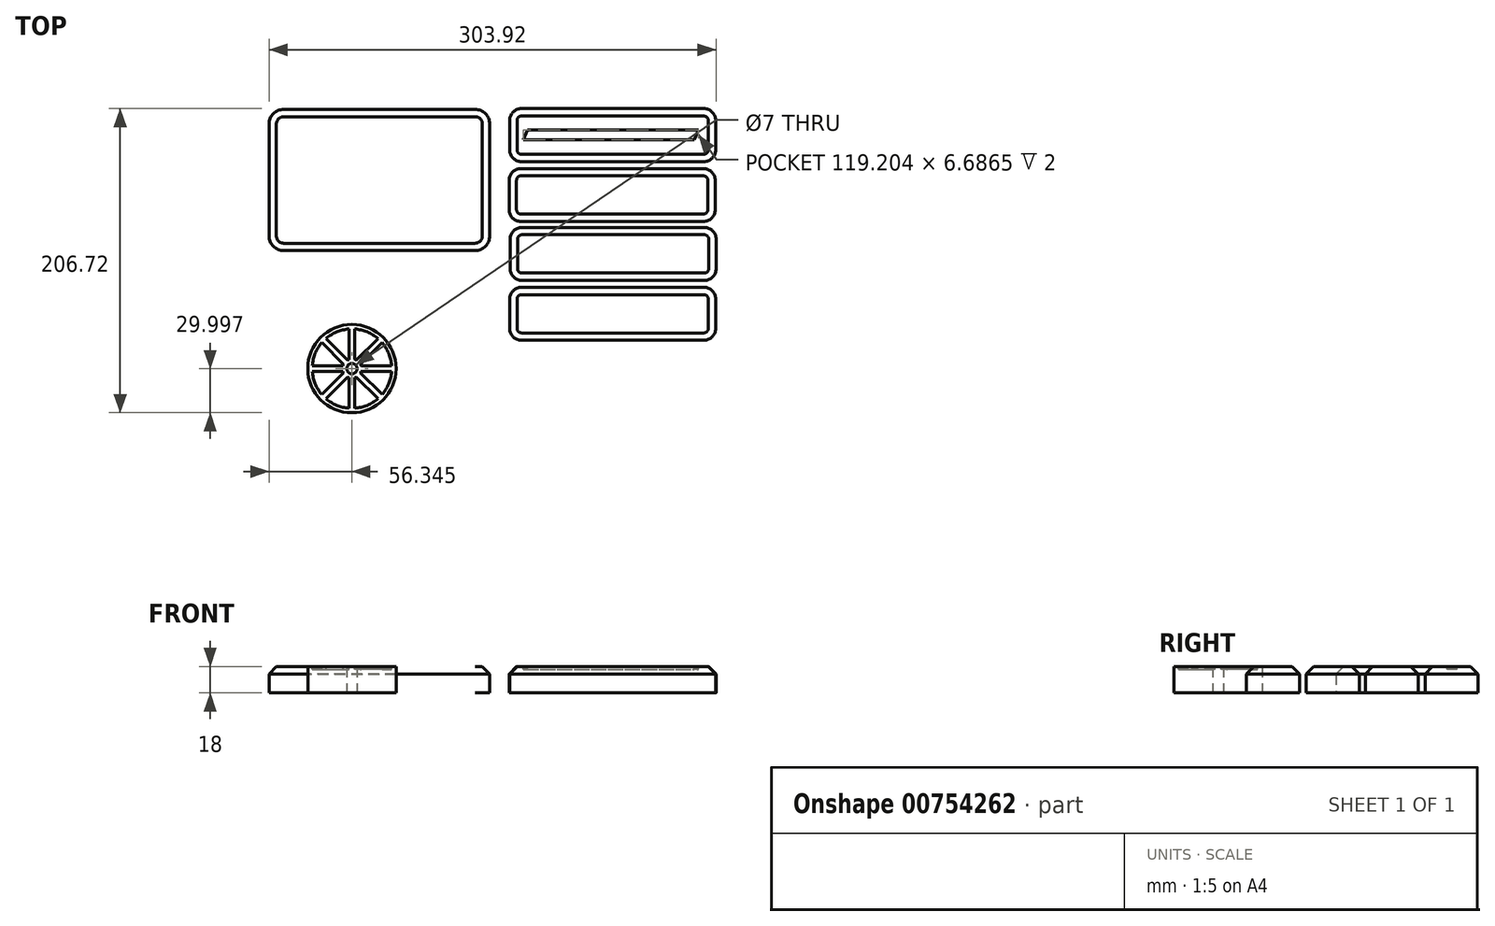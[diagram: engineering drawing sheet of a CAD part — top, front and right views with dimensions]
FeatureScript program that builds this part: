
annotation { "Feature Type Name" : "Feature", "Feature Type Description" : "" }
export const myFeature = defineFeature(function(context is Context, id is Id, definition is map)
    precondition{}
    {
        {
            var Q0;
            Q0=qCreatedBy(makeId("Top.planeOp"),FACE);
            var sketch = newSketch(context, id + "F0", { "sketchPlane" : qUnion([Q0])});
            skLineSegment(sketch, "E0.bottom", {"start": v(-76.14, 52.3) * mm, "end": v(53.86, 52.3) * mm});
            skLineSegment(sketch, "E0.top", {"start": v(-76.14, -43.7) * mm, "end": v(53.86, -43.7) * mm});
            skLineSegment(sketch, "E0.left", {"start": v(-86.14, 42.3) * mm, "end": v(-86.14, -33.7) * mm});
            skLineSegment(sketch, "E0.right", {"start": v(63.86, 42.3) * mm, "end": v(63.86, -33.7) * mm});
            skPoint(sketch, "E1.visualSharp", {"position": v(-86.14, 52.3) * mm});
            skArc(sketch, "E1.filletArc", {"start": v(-76.14, 52.3) * mm, "mid": v(-83.2, 49.38) * mm, "end": v(-86.14, 42.3) * mm});
            skPoint(sketch, "E2.visualSharp", {"position": v(-86.14, -43.7) * mm});
            skArc(sketch, "E2.filletArc", {"start": v(-86.14, -33.7) * mm, "mid": v(-83.2, -40.77) * mm, "end": v(-76.14, -43.7) * mm});
            skPoint(sketch, "E3.visualSharp", {"position": v(63.86, -43.7) * mm});
            skArc(sketch, "E3.filletArc", {"start": v(53.86, -43.7) * mm, "mid": v(60.93, -40.77) * mm, "end": v(63.86, -33.7) * mm});
            skPoint(sketch, "E4.visualSharp", {"position": v(63.86, 52.3) * mm});
            skArc(sketch, "E4.filletArc", {"start": v(63.86, 42.3) * mm, "mid": v(60.93, 49.38) * mm, "end": v(53.86, 52.3) * mm});
            skLineSegment(sketch, "E5.bottom", {"start": v(85.44, 52.8) * mm, "end": v(209.44, 52.8) * mm});
            skLineSegment(sketch, "E5.top", {"start": v(85.44, 16.8) * mm, "end": v(209.44, 16.8) * mm});
            skLineSegment(sketch, "E5.left", {"start": v(77.44, 44.8) * mm, "end": v(77.44, 24.8) * mm});
            skLineSegment(sketch, "E5.right", {"start": v(217.44, 44.8) * mm, "end": v(217.44, 24.8) * mm});
            skPoint(sketch, "E6.visualSharp", {"position": v(77.44, 52.8) * mm});
            skArc(sketch, "E6.filletArc", {"start": v(85.44, 52.8) * mm, "mid": v(79.79, 50.45) * mm, "end": v(77.44, 44.8) * mm});
            skPoint(sketch, "E7.visualSharp", {"position": v(77.44, 16.8) * mm});
            skArc(sketch, "E7.filletArc", {"start": v(77.44, 24.8) * mm, "mid": v(79.79, 19.14) * mm, "end": v(85.44, 16.8) * mm});
            skPoint(sketch, "E8.visualSharp", {"position": v(217.44, 16.8) * mm});
            skArc(sketch, "E8.filletArc", {"start": v(209.44, 16.8) * mm, "mid": v(215.1, 19.14) * mm, "end": v(217.44, 24.8) * mm});
            skPoint(sketch, "E9.visualSharp", {"position": v(217.44, 52.8) * mm});
            skArc(sketch, "E9.filletArc", {"start": v(217.44, 44.8) * mm, "mid": v(215.1, 50.45) * mm, "end": v(209.44, 52.8) * mm});
            skLineSegment(sketch, "E10.bottom", {"start": v(85.1, 12.1) * mm, "end": v(209.1, 12.1) * mm});
            skLineSegment(sketch, "E10.top", {"start": v(85.1, -23.9) * mm, "end": v(209.1, -23.9) * mm});
            skLineSegment(sketch, "E10.left", {"start": v(77.1, 4.1) * mm, "end": v(77.1, -15.9) * mm});
            skLineSegment(sketch, "E10.right", {"start": v(217.1, 4.1) * mm, "end": v(217.1, -15.9) * mm});
            skPoint(sketch, "E11.visualSharp", {"position": v(77.1, 12.1) * mm});
            skArc(sketch, "E11.filletArc", {"start": v(85.1, 12.1) * mm, "mid": v(79.45, 9.76) * mm, "end": v(77.1, 4.1) * mm});
            skPoint(sketch, "E12.visualSharp", {"position": v(77.1, -23.9) * mm});
            skArc(sketch, "E12.filletArc", {"start": v(77.1, -15.9) * mm, "mid": v(79.45, -21.55) * mm, "end": v(85.1, -23.9) * mm});
            skPoint(sketch, "E13.visualSharp", {"position": v(217.1, -23.9) * mm});
            skArc(sketch, "E13.filletArc", {"start": v(209.1, -23.9) * mm, "mid": v(214.76, -21.55) * mm, "end": v(217.1, -15.9) * mm});
            skPoint(sketch, "E14.visualSharp", {"position": v(217.1, 12.1) * mm});
            skArc(sketch, "E14.filletArc", {"start": v(217.1, 4.1) * mm, "mid": v(214.76, 9.76) * mm, "end": v(209.1, 12.1) * mm});
            skLineSegment(sketch, "E15.bottom", {"start": v(85.78, -27.97) * mm, "end": v(209.78, -27.97) * mm});
            skLineSegment(sketch, "E15.top", {"start": v(85.78, -63.97) * mm, "end": v(209.78, -63.97) * mm});
            skLineSegment(sketch, "E15.left", {"start": v(77.78, -35.97) * mm, "end": v(77.78, -55.97) * mm});
            skLineSegment(sketch, "E15.right", {"start": v(217.78, -35.97) * mm, "end": v(217.78, -55.97) * mm});
            skPoint(sketch, "E16.visualSharp", {"position": v(77.78, -27.97) * mm});
            skArc(sketch, "E16.filletArc", {"start": v(85.78, -27.97) * mm, "mid": v(80.13, -30.3) * mm, "end": v(77.78, -35.97) * mm});
            skPoint(sketch, "E17.visualSharp", {"position": v(77.78, -63.97) * mm});
            skArc(sketch, "E17.filletArc", {"start": v(77.78, -55.97) * mm, "mid": v(80.13, -61.62) * mm, "end": v(85.78, -63.97) * mm});
            skPoint(sketch, "E18.visualSharp", {"position": v(217.78, -63.97) * mm});
            skArc(sketch, "E18.filletArc", {"start": v(209.78, -63.97) * mm, "mid": v(215.44, -61.62) * mm, "end": v(217.78, -55.97) * mm});
            skPoint(sketch, "E19.visualSharp", {"position": v(217.78, -27.97) * mm});
            skArc(sketch, "E19.filletArc", {"start": v(217.78, -35.97) * mm, "mid": v(215.44, -30.3) * mm, "end": v(209.78, -27.97) * mm});
            skLineSegment(sketch, "E20.bottom", {"start": v(85.44, -68.65) * mm, "end": v(209.44, -68.65) * mm});
            skLineSegment(sketch, "E20.top", {"start": v(85.44, -104.65) * mm, "end": v(209.44, -104.65) * mm});
            skLineSegment(sketch, "E20.left", {"start": v(77.44, -76.65) * mm, "end": v(77.44, -96.65) * mm});
            skLineSegment(sketch, "E20.right", {"start": v(217.44, -76.65) * mm, "end": v(217.44, -96.65) * mm});
            skPoint(sketch, "E21.visualSharp", {"position": v(77.44, -68.65) * mm});
            skArc(sketch, "E21.filletArc", {"start": v(85.44, -68.65) * mm, "mid": v(79.79, -71) * mm, "end": v(77.44, -76.65) * mm});
            skPoint(sketch, "E22.visualSharp", {"position": v(77.44, -104.65) * mm});
            skArc(sketch, "E22.filletArc", {"start": v(77.44, -96.65) * mm, "mid": v(79.79, -102.31) * mm, "end": v(85.44, -104.65) * mm});
            skPoint(sketch, "E23.visualSharp", {"position": v(217.44, -104.65) * mm});
            skArc(sketch, "E23.filletArc", {"start": v(209.44, -104.65) * mm, "mid": v(215.1, -102.31) * mm, "end": v(217.44, -96.65) * mm});
            skPoint(sketch, "E24.visualSharp", {"position": v(217.44, -68.65) * mm});
            skArc(sketch, "E24.filletArc", {"start": v(217.44, -76.65) * mm, "mid": v(215.1, -71) * mm, "end": v(209.44, -68.65) * mm});
            skSolve(sketch);
        }
        {
            var Q0;
            Q0 = qSketchRegion(id + "F0", true);
            extrude(context, id + "F1", {"entities" : qUnion([Q0]), "depth" : 18 * mm, "offsetDistance" : 25 * mm});
        }
        {
            var Q0;
            Q0=makeQuery(id+"F1.opExtrude","CAP_FACE",FACE,{"disambiguationData":[OSD([sQuery(id+"F0.wireOp",EDGE,"E0.bottom"),sQuery(id+"F0.wireOp",EDGE,"E0.top"),sQuery(id+"F0.wireOp",EDGE,"E0.left"),sQuery(id+"F0.wireOp",EDGE,"E0.right"),sQuery(id+"F0.wireOp",EDGE,"E1.filletArc"),sQuery(id+"F0.wireOp",EDGE,"E2.filletArc"),sQuery(id+"F0.wireOp",EDGE,"E3.filletArc"),sQuery(id+"F0.wireOp",EDGE,"E4.filletArc")])],"isStart":false});
            var Q1;
            Q1=makeQuery(id+"F1.opExtrude","CAP_FACE",FACE,{"disambiguationData":[OSD([sQuery(id+"F0.wireOp",EDGE,"E5.bottom"),sQuery(id+"F0.wireOp",EDGE,"E5.top"),sQuery(id+"F0.wireOp",EDGE,"E5.left"),sQuery(id+"F0.wireOp",EDGE,"E5.right"),sQuery(id+"F0.wireOp",EDGE,"E6.filletArc"),sQuery(id+"F0.wireOp",EDGE,"E7.filletArc"),sQuery(id+"F0.wireOp",EDGE,"E8.filletArc"),sQuery(id+"F0.wireOp",EDGE,"E9.filletArc")])],"isStart":false});
            var Q2;
            Q2=makeQuery(id+"F1.opExtrude","CAP_FACE",FACE,{"disambiguationData":[OSD([sQuery(id+"F0.wireOp",EDGE,"E10.bottom"),sQuery(id+"F0.wireOp",EDGE,"E10.top"),sQuery(id+"F0.wireOp",EDGE,"E10.left"),sQuery(id+"F0.wireOp",EDGE,"E10.right"),sQuery(id+"F0.wireOp",EDGE,"E11.filletArc"),sQuery(id+"F0.wireOp",EDGE,"E12.filletArc"),sQuery(id+"F0.wireOp",EDGE,"E13.filletArc"),sQuery(id+"F0.wireOp",EDGE,"E14.filletArc")])],"isStart":false});
            var Q3;
            Q3=makeQuery(id+"F1.opExtrude","CAP_FACE",FACE,{"disambiguationData":[OSD([sQuery(id+"F0.wireOp",EDGE,"E15.bottom"),sQuery(id+"F0.wireOp",EDGE,"E15.top"),sQuery(id+"F0.wireOp",EDGE,"E15.left"),sQuery(id+"F0.wireOp",EDGE,"E15.right"),sQuery(id+"F0.wireOp",EDGE,"E16.filletArc"),sQuery(id+"F0.wireOp",EDGE,"E17.filletArc"),sQuery(id+"F0.wireOp",EDGE,"E18.filletArc"),sQuery(id+"F0.wireOp",EDGE,"E19.filletArc")])],"isStart":false});
            var Q4;
            Q4=makeQuery(id+"F1.opExtrude","CAP_FACE",FACE,{"disambiguationData":[OSD([sQuery(id+"F0.wireOp",EDGE,"E20.bottom"),sQuery(id+"F0.wireOp",EDGE,"E20.top"),sQuery(id+"F0.wireOp",EDGE,"E20.left"),sQuery(id+"F0.wireOp",EDGE,"E20.right"),sQuery(id+"F0.wireOp",EDGE,"E21.filletArc"),sQuery(id+"F0.wireOp",EDGE,"E22.filletArc"),sQuery(id+"F0.wireOp",EDGE,"E23.filletArc"),sQuery(id+"F0.wireOp",EDGE,"E24.filletArc")])],"isStart":false});
            chamfer(context, id + "F2", {"entities" : qUnion([Q0, Q1, Q2, Q3, Q4]), "width" : 5 * mm, "tangentPropagation" : true});
        }
        {
            var Q0;
            Q0=makeQuery(id+"F1.opExtrude","CAP_FACE",FACE,{"disambiguationData":[OSD([sQuery(id+"F0.wireOp",EDGE,"E5.bottom"),sQuery(id+"F0.wireOp",EDGE,"E5.top"),sQuery(id+"F0.wireOp",EDGE,"E5.left"),sQuery(id+"F0.wireOp",EDGE,"E5.right"),sQuery(id+"F0.wireOp",EDGE,"E6.filletArc"),sQuery(id+"F0.wireOp",EDGE,"E7.filletArc"),sQuery(id+"F0.wireOp",EDGE,"E8.filletArc"),sQuery(id+"F0.wireOp",EDGE,"E9.filletArc")])],"isStart":false});
            var sketch = newSketch(context, id + "F3", { "sketchPlane" : qUnion([Q0])});
            skSolve(sketch);
        }
        {
            var Q0;
            {var subQ0=sQuery(id+"F0.wireOp",EDGE,"E9.filletArc");var subQ1=sQuery(id+"F0.wireOp",EDGE,"E8.filletArc");var subQ2=sQuery(id+"F0.wireOp",EDGE,"E7.filletArc");var subQ3=sQuery(id+"F0.wireOp",EDGE,"E6.filletArc");var subQ4=sQuery(id+"F0.wireOp",EDGE,"E5.right");var subQ5=sQuery(id+"F0.wireOp",EDGE,"E5.left");var subQ6=sQuery(id+"F0.wireOp",EDGE,"E5.top");var subQ7=sQuery(id+"F0.wireOp",EDGE,"E5.bottom");var subQ8=makeQuery(id+"F1.opExtrude","CAP_FACE",FACE,{"disambiguationData":[OSD([subQ7,subQ6,subQ5,subQ4,subQ3,subQ2,subQ1,subQ0])],"isStart":false});Q0=makeQuery(id+"F3.imprint","IMPRINT",FACE,{"disambiguationData":[TD([[makeQuery(id+"F3.imprint","IMPRINT",EDGE,{"derivedFrom":makeQuery(id+"F2.opChamfer","BLEND_EDGE",EDGE,{"blendedFrom":[makeQuery(id+"F1.opExtrude","CAP_EDGE",EDGE,{"disambiguationData":[OSD([subQ7])],"isStart":false}),subQ8],"blendedInto":[subQ8]})}),1.0]])]});}
            var sketch = newSketch(context, id + "F4", { "sketchPlane" : qUnion([Q0])});
            skLineSegment(sketch, "E25", {"start": v(212.5, 34.8) * mm, "end": v(82.44, 34.8) * mm, "construction": true});
            skLineSegment(sketch, "E26", {"start": v(89.67, 38.44) * mm, "end": v(86.67, 31.75) * mm});
            skLineSegment(sketch, "E27", {"start": v(89.67, 38.44) * mm, "end": v(205.88, 38.44) * mm});
            skLineSegment(sketch, "E28", {"start": v(86.67, 31.75) * mm, "end": v(202.87, 31.75) * mm});
            skLineSegment(sketch, "E29", {"start": v(205.88, 38.44) * mm, "end": v(202.87, 31.75) * mm});
            skSolve(sketch);
        }
        {
            var Q0;
            Q0 = qSketchRegion(id + "F4", true);
            extrude(context, id + "F5", {"entities" : qUnion([Q0]), "operationType" : NewBodyOperationType.REMOVE, "oppositeDirection" : true, "depth" : 2 * mm, "offsetDistance" : 25 * mm});
        }
        {
            var Q0;
            Q0=qCreatedBy(makeId("Top.planeOp"),FACE);
            var sketch = newSketch(context, id + "F6", { "sketchPlane" : qUnion([Q0])});
            skCircle(sketch, "E30", {"center": v(-29.8, -123.92) * mm, "radius": 30 * mm});
            skCircle(sketch, "E31", {"center": v(-29.8, -123.92) * mm, "radius": 3.5 * mm});
            skSolve(sketch);
        }
        {
            var Q0;
            Q0 = qSketchRegion(id + "F6", true);
            extrude(context, id + "F7", {"entities" : qUnion([Q0]), "depth" : 18 * mm, "offsetDistance" : 25 * mm});
        }
        {
            var Q0;
            Q0=makeQuery(id+"F7.opExtrude","CAP_FACE",FACE,{"disambiguationData":[OSD([sQuery(id+"F6.wireOp",EDGE,"E30"),sQuery(id+"F6.wireOp",EDGE,"E31")])],"isStart":false});
            var sketch = newSketch(context, id + "F8", { "sketchPlane" : qUnion([Q0])});
            skArc(sketch, "E32", {"start": v(-12.17, -103.47) * mm, "mid": v(-19.46, -98.98) * mm, "end": v(-27.8, -97) * mm});
            skArc(sketch, "E33", {"start": v(-26.84, -118.14) * mm, "mid": v(-27.3, -117.92) * mm, "end": v(-27.8, -117.74) * mm});
            skLineSegment(sketch, "E34", {"start": v(-29.8, -123.92) * mm, "end": v(-29.8, -96.92) * mm, "construction": true});
            skLineSegment(sketch, "E35", {"start": v(-29.8, -123.92) * mm, "end": v(-2.8, -123.92) * mm, "construction": true});
            skLineSegment(sketch, "E36", {"start": v(-29.8, -123.92) * mm, "end": v(-10.7, -104.83) * mm, "construction": true});
            skLineSegment(sketch, "E37", {"start": v(-27.8, -97) * mm, "end": v(-27.8, -117.74) * mm});
            skLineSegment(sketch, "E38", {"start": v(-12.17, -103.47) * mm, "end": v(-26.84, -118.14) * mm});
            skArc(sketch, "E39.trimOffspring", {"start": v(-31.8, -117.74) * mm, "mid": v(-32.28, -117.92) * mm, "end": v(-32.75, -118.14) * mm, "construction": true});
            skArc(sketch, "E40.MirrorCS", {"start": v(-32.75, -118.14) * mm, "mid": v(-32.28, -117.92) * mm, "end": v(-31.8, -117.74) * mm});
            skLineSegment(sketch, "E41.MirrorCS", {"start": v(-31.8, -97) * mm, "end": v(-31.8, -117.74) * mm});
            skLineSegment(sketch, "E42.MirrorCS", {"start": v(-47.42, -103.47) * mm, "end": v(-32.75, -118.14) * mm});
            skArc(sketch, "E43.MirrorCS", {"start": v(-47.42, -103.47) * mm, "mid": v(-40.13, -98.98) * mm, "end": v(-31.8, -97) * mm});
            skArc(sketch, "E44.MirrorCS", {"start": v(-9.34, -106.3) * mm, "mid": v(-4.85, -113.6) * mm, "end": v(-2.87, -121.92) * mm});
            skLineSegment(sketch, "E45.MirrorCS", {"start": v(-9.34, -106.3) * mm, "end": v(-24, -120.96) * mm});
            skArc(sketch, "E46.MirrorCS", {"start": v(-24, -120.96) * mm, "mid": v(-23.79, -121.44) * mm, "end": v(-23.61, -121.92) * mm});
            skLineSegment(sketch, "E47.MirrorCS", {"start": v(-2.87, -121.92) * mm, "end": v(-23.61, -121.92) * mm});
            skLineSegment(sketch, "E48.MirrorCS", {"start": v(-9.34, -141.55) * mm, "end": v(-24, -126.88) * mm});
            skLineSegment(sketch, "E49.MirrorCS", {"start": v(-2.87, -125.92) * mm, "end": v(-23.61, -125.92) * mm});
            skArc(sketch, "E50.MirrorCS", {"start": v(-23.61, -125.92) * mm, "mid": v(-23.79, -126.41) * mm, "end": v(-24, -126.88) * mm});
            skArc(sketch, "E51.MirrorCS", {"start": v(-9.34, -141.55) * mm, "mid": v(-4.85, -134.26) * mm, "end": v(-2.87, -125.92) * mm});
            skArc(sketch, "E52.trimOffspring", {"start": v(-23.61, -121.92) * mm, "mid": v(-23.79, -121.44) * mm, "end": v(-24, -120.96) * mm});
            skPoint(sketch, "E53.orphan", {"position": v(-25.2, -119.33) * mm});
            skPoint(sketch, "E54.orphan", {"position": v(-23.3, -123.92) * mm});
            skArc(sketch, "E55.trimOffspring", {"start": v(-27.8, -117.74) * mm, "mid": v(-27.3, -117.92) * mm, "end": v(-26.84, -118.14) * mm});
            skPoint(sketch, "E56.orphan", {"position": v(-29.8, -117.42) * mm});
            skArc(sketch, "E57.trimOffspring", {"start": v(-24, -126.88) * mm, "mid": v(-23.79, -126.41) * mm, "end": v(-23.61, -125.92) * mm, "construction": true});
            skArc(sketch, "E58.MirrorCS", {"start": v(-12.17, -144.38) * mm, "mid": v(-19.46, -148.87) * mm, "end": v(-27.8, -150.85) * mm});
            skArc(sketch, "E59.MirrorCS", {"start": v(-47.42, -144.38) * mm, "mid": v(-40.13, -148.87) * mm, "end": v(-31.8, -150.85) * mm});
            skLineSegment(sketch, "E60.MirrorCS", {"start": v(-47.42, -144.38) * mm, "end": v(-32.75, -129.71) * mm});
            skLineSegment(sketch, "E61.MirrorCS", {"start": v(-31.8, -150.85) * mm, "end": v(-31.8, -130.1) * mm});
            skLineSegment(sketch, "E62.MirrorCS", {"start": v(-27.8, -150.85) * mm, "end": v(-27.8, -130.1) * mm});
            skLineSegment(sketch, "E63.MirrorCS", {"start": v(-12.17, -144.38) * mm, "end": v(-26.84, -129.71) * mm});
            skArc(sketch, "E64.MirrorCS", {"start": v(-27.8, -130.1) * mm, "mid": v(-27.3, -129.93) * mm, "end": v(-26.84, -129.71) * mm});
            skArc(sketch, "E65.MirrorCS", {"start": v(-32.75, -129.71) * mm, "mid": v(-32.28, -129.93) * mm, "end": v(-31.8, -130.1) * mm});
            skLineSegment(sketch, "E66", {"start": v(-29.8, -123.92) * mm, "end": v(-8.58, -145.14) * mm, "construction": true});
            skArc(sketch, "E67.MirrorCS", {"start": v(-35.98, -125.92) * mm, "mid": v(-35.8, -126.41) * mm, "end": v(-35.58, -126.88) * mm});
            skArc(sketch, "E68.MirrorCS", {"start": v(-35.98, -121.92) * mm, "mid": v(-35.8, -121.44) * mm, "end": v(-35.58, -120.96) * mm});
            skLineSegment(sketch, "E69.MirrorCS", {"start": v(-50.25, -141.55) * mm, "end": v(-35.58, -126.88) * mm});
            skArc(sketch, "E70.MirrorCS", {"start": v(-50.25, -141.55) * mm, "mid": v(-54.74, -134.26) * mm, "end": v(-56.72, -125.92) * mm});
            skLineSegment(sketch, "E71.MirrorCS", {"start": v(-56.72, -125.92) * mm, "end": v(-35.98, -125.92) * mm});
            skLineSegment(sketch, "E72.MirrorCS", {"start": v(-50.25, -106.3) * mm, "end": v(-35.58, -120.96) * mm});
            skLineSegment(sketch, "E73.MirrorCS", {"start": v(-56.72, -121.92) * mm, "end": v(-35.98, -121.92) * mm});
            skArc(sketch, "E74.MirrorCS", {"start": v(-50.25, -106.3) * mm, "mid": v(-54.74, -113.6) * mm, "end": v(-56.72, -121.92) * mm});
            skSolve(sketch);
        }
        {
            var Q0;
            Q0 = qSketchRegion(id + "F8", true);
            extrude(context, id + "F9", {"entities" : qUnion([Q0]), "operationType" : NewBodyOperationType.REMOVE, "oppositeDirection" : true, "depth" : 2 * mm, "offsetDistance" : 25 * mm});
        }
    });
